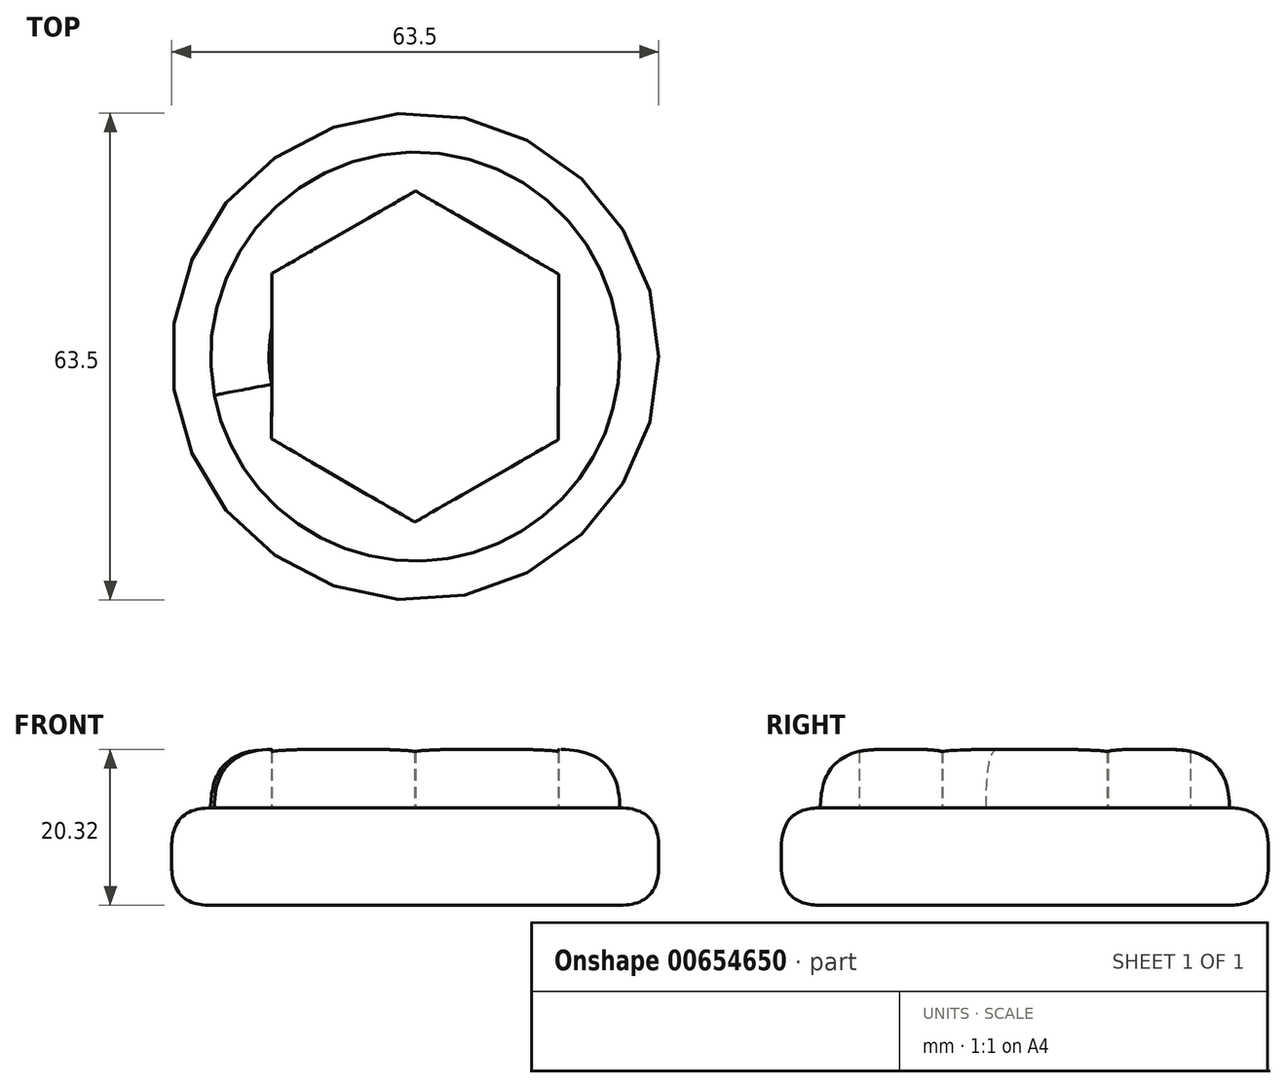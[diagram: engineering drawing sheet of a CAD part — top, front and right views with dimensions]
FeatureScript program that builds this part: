
annotation { "Feature Type Name" : "Feature", "Feature Type Description" : "" }
export const myFeature = defineFeature(function(context is Context, id is Id, definition is map)
    precondition{}
    {
        {
            var Q0;
            Q0=qCreatedBy(makeId("Top.planeOp"),FACE);
            var sketch = newSketch(context, id + "F0", { "sketchPlane" : qUnion([Q0])});
            skCircle(sketch, "E0", {"center": v(0, 0) * mm, "radius": 31.75 * mm});
            skSolve(sketch);
        }
        {
            var Q0;
            Q0 = qSketchRegion(id + "F0", true);
            extrude(context, id + "F1", {"entities" : qUnion([Q0]), "depth" : 12.7 * mm, "offsetDistance" : 25.4 * mm});
        }
        {
            var Q0;
            Q0=makeQuery(id+"F1.opExtrude","CAP_EDGE",EDGE,{"disambiguationData":[OSD([sQuery(id+"F0.wireOp",EDGE,"E0")])],"isStart":false});
            var Q1;
            Q1=makeQuery(id+"F1.opExtrude","CAP_EDGE",EDGE,{"disambiguationData":[OSD([sQuery(id+"F0.wireOp",EDGE,"E0")])],"isStart":true});
            fillet(context, id + "F2", {"entities" : qUnion([Q0, Q1]), "radius" : 5.08 * mm, "tangentPropagation" : true, "rho" : .5, "crossSection" : FilletCrossSection.CONIC, "allowEdgeOverflow" : false});
        }
        {
            var Q0;
            Q0=makeQuery(id+"F1.opExtrude","CAP_FACE",FACE,{"disambiguationData":[OSD([sQuery(id+"F0.wireOp",EDGE,"E0")])],"isStart":false});
            var sketch = newSketch(context, id + "F3", { "sketchPlane" : qUnion([Q0])});
            skCircle(sketch, "E1.cCircle", {"center": v(0, 0) * mm, "radius": 18.7 * mm, "construction": true});
            skLineSegment(sketch, "E1.0", {"start": v(18.67, -10.84) * mm, "end": v(-0.05, -21.59) * mm});
            skLineSegment(sketch, "E1.1", {"start": v(-0.05, -21.59) * mm, "end": v(-18.72, -10.75) * mm});
            skLineSegment(sketch, "E1.2", {"start": v(-18.72, -10.75) * mm, "end": v(-18.67, 10.84) * mm});
            skLineSegment(sketch, "E1.3", {"start": v(-18.67, 10.84) * mm, "end": v(0.05, 21.59) * mm});
            skLineSegment(sketch, "E1.4", {"start": v(0.05, 21.59) * mm, "end": v(18.72, 10.75) * mm});
            skLineSegment(sketch, "E1.5", {"start": v(18.72, 10.75) * mm, "end": v(18.67, -10.84) * mm});
            skPoint(sketch, "E1.0.midPoint", {"position": v(9.3, -16.21) * mm});
            skSolve(sketch);
        }
        {
            var Q0;
            Q0=makeQuery(id+"F3.imprint","IMPRINT",FACE,{"disambiguationData":[TD([[makeQuery(id+"F3.imprint","IMPRINT",EDGE,{"derivedFrom":sQuery(id+"F3.wireOp",EDGE,"E1.0")}),1.0]])]});
            extrude(context, id + "F4", {"entities" : qUnion([Q0]), "operationType" : NewBodyOperationType.ADD, "depth" : 7.62 * mm, "offsetDistance" : 25.4 * mm});
        }
        {
            var Q0;
            Q0=makeQuery(id+"F4.opExtrude","CAP_EDGE",EDGE,{"disambiguationData":[OSD([sQuery(id+"F0.wireOp",EDGE,"E0")])],"isStart":false});
            fillet(context, id + "F5", {"entities" : qUnion([Q0]), "radius" : 7.62 * mm, "tangentPropagation" : true, "rho" : 0.5, "crossSection" : FilletCrossSection.CONIC, "allowEdgeOverflow" : false});
        }
    });
